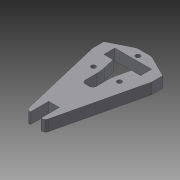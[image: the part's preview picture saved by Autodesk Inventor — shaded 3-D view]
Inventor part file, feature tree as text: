
AUTODESK INVENTOR PART (.ipt)
format: ipt  version: 2015 (Build 190159000, 159)  size: 166,912 bytes
history: native  units: mm
features: extrude x2, sketch x1
ambient origin geometry x8: Origin, YZ Plane, XZ Plane, XY Plane, X Axis, Y Axis, Z Axis, Center Point
bodies: Body1 (feature_tree)
feature tree (3):
  extrude  "Extrusion7"  Depth=20.0mm
  extrude  "Extrusion8"  Depth=5.8mm
  sketch  "Sketch1"  dims[d59=15.0mm d69=20.0mm d88=5.8mm d95=2.0mm d96=2.0mm d97=10.0mm d98=10.0mm d109=43.0mm d112=2.5mm d113=2.5mm d114=2.5mm d123=32.0mm d126=8.0mm d127=4.0mm d130=6.0mm d131=0.0mm d132=6.0mm d134=6.0mm d135=6.0mm d142=6.0mm d143=0.0mm d144=16.0mm d145=35.5mm d148=5.0mm d149=5.0mm d153=6.0mm d155=6.0mm d156=135.0deg d157=25.0mm d160=6.0mm d161=20.0mm d162=2.0mm d163=2.0mm d169=30.5mm]
